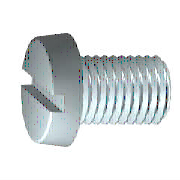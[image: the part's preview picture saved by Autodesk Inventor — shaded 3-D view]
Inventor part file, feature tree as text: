
AUTODESK INVENTOR PART (.ipt)
format: ipt  version: 2023.2 (Build 272271030, 271C)  size: 178,176 bytes
history: native  units: mm (DEFAULTED — no unit token found)
features: sketch x2, extrude x1, plane x1
ambient origin geometry x7: Origin, YZ Plane, XZ Plane, X Axis, Y Axis, Z Axis, Center Point
bodies: Solid1 (feature_tree), Body (feature_tree)
feature tree (4):
  sketch  "Sketch2"  dims[d2=0.49086mm d3=3.3mm d4=5.0mm d5=4.566987mm d8=90.0deg d7=0.0mm d9=8.5mm d10=0.872665mm d11=1.2mm d12=8.5mm d14=0.2mm d15=48.4mm d16=0.0mm d17=0.433015mm d18=0.49086mm d19=1.3mm d20=0.0mm d36=45.0deg d37=0.0mm d39=0.0mm]
  extrude  "Slot"  Depth=48.4mm
  plane  "Work Plane1"
  sketch  "Sketch1"  dims[d0=50.0mm d1=48.4mm]
